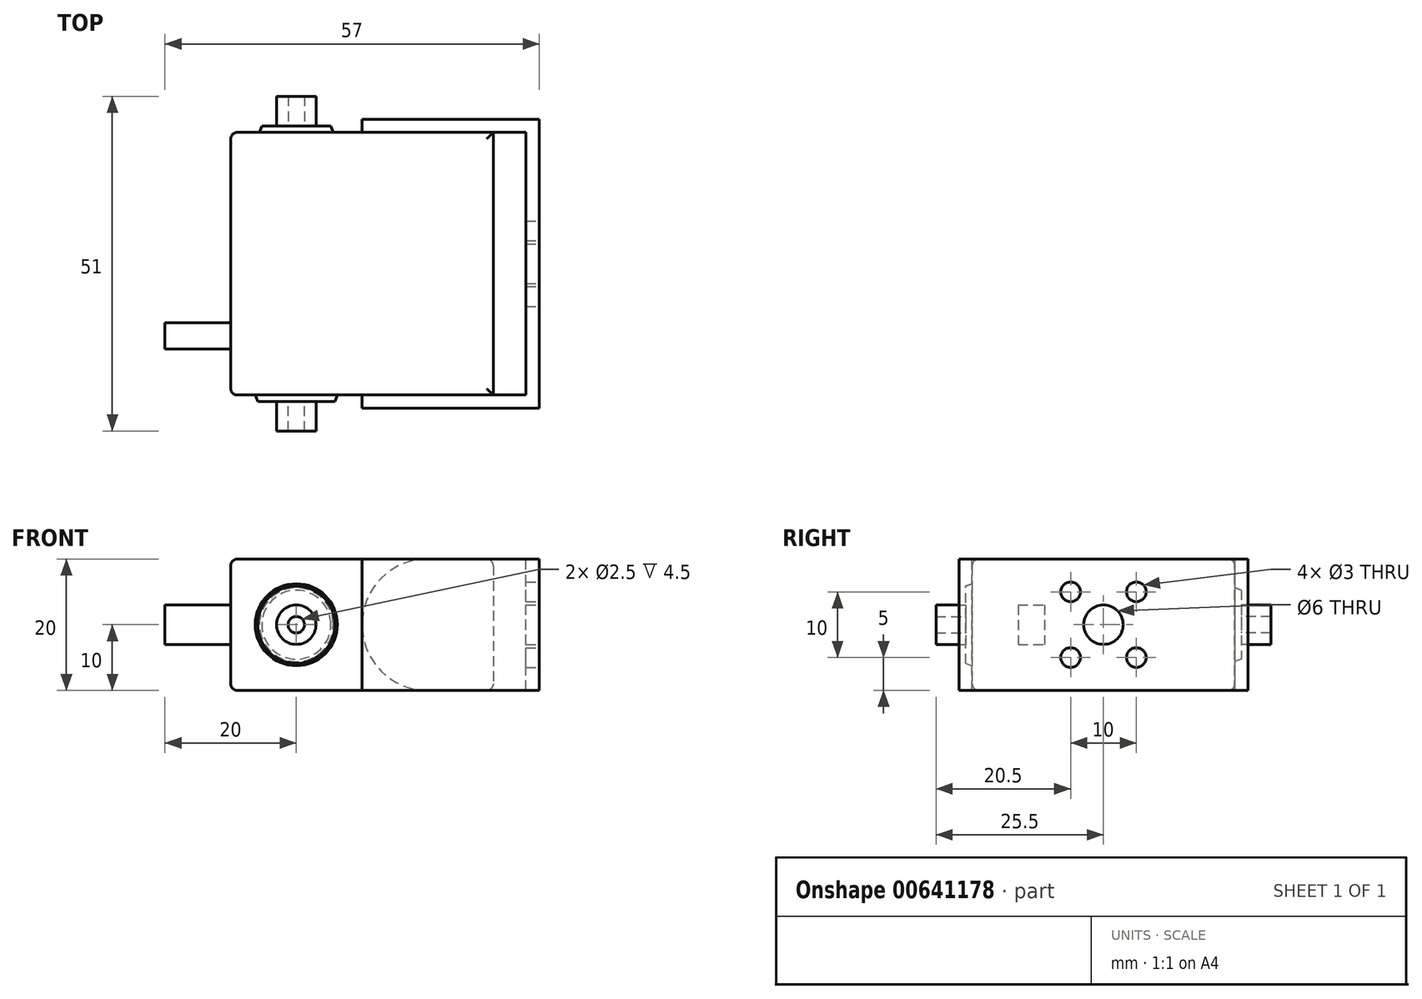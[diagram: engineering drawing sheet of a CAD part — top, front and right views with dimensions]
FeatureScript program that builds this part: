
annotation { "Feature Type Name" : "Feature", "Feature Type Description" : "" }
export const myFeature = defineFeature(function(context is Context, id is Id, definition is map)
    precondition{}
    {
        {
            var Q0;
            Q0=qCreatedBy(makeId("Top.planeOp"),FACE);
            var sketch = newSketch(context, id + "F0", { "sketchPlane" : qUnion([Q0])});
            skLineSegment(sketch, "E0.bottom", {"start": v(0, 0) * mm, "end": v(40, 0) * mm});
            skLineSegment(sketch, "E0.top", {"start": v(0, -40) * mm, "end": v(40, -40) * mm});
            skLineSegment(sketch, "E0.left", {"start": v(0, 0) * mm, "end": v(0, -40) * mm});
            skLineSegment(sketch, "E0.right", {"start": v(40, 0) * mm, "end": v(40, -40) * mm});
            skSolve(sketch);
        }
        {
            var Q0;
            Q0=makeQuery(id+"F0.imprint","IMPRINT",FACE,{"disambiguationData":[TD([[makeQuery(id+"F0.imprint","IMPRINT",EDGE,{"derivedFrom":sQuery(id+"F0.wireOp",EDGE,"E0.bottom")}),-1.0]])]});
            extrude(context, id + "F1", {"entities" : qUnion([Q0]), "depth" : 20 * mm, "offsetDistance" : 25 * mm});
        }
        {
            var Q0;
            Q0=makeQuery(id+"F1.opExtrude","CAP_FACE",FACE,{"disambiguationData":[OSD([sQuery(id+"F0.wireOp",EDGE,"E0.bottom"),sQuery(id+"F0.wireOp",EDGE,"E0.top"),sQuery(id+"F0.wireOp",EDGE,"E0.left"),sQuery(id+"F0.wireOp",EDGE,"E0.right")])],"isStart":false});
            var sketch = newSketch(context, id + "F2", { "sketchPlane" : qUnion([Q0])});
            skLineSegment(sketch, "E1", {"start": v(20, 0) * mm, "end": v(20, 2) * mm});
            skLineSegment(sketch, "E2", {"start": v(20, 2) * mm, "end": v(47, 2) * mm});
            skLineSegment(sketch, "E3", {"start": v(47, 2) * mm, "end": v(47, -42) * mm});
            skLineSegment(sketch, "E4", {"start": v(47, -42) * mm, "end": v(20, -42) * mm});
            skLineSegment(sketch, "E5", {"start": v(20, -42) * mm, "end": v(20, -40) * mm});
            skLineSegment(sketch, "E6", {"start": v(20, -40) * mm, "end": v(45, -40) * mm});
            skLineSegment(sketch, "E7", {"start": v(45, -40) * mm, "end": v(45, 0) * mm});
            skLineSegment(sketch, "E8", {"start": v(45, 0) * mm, "end": v(20, 0) * mm});
            skSolve(sketch);
        }
        {
            var Q0;
            {var subQ0=sQuery(id+"F2.wireOp",EDGE,"E1");Q0=makeQuery(id+"F2.imprint","IMPRINT",FACE,{"disambiguationData":[TD([[makeQuery(id+"F2.imprint","IMPRINT",EDGE,{"derivedFrom":subQ0}),-1.0]])]});}
            extrude(context, id + "F3", {"entities" : qUnion([Q0]), "oppositeDirection" : true, "depth" : 20 * mm, "offsetDistance" : 25 * mm});
        }
        {
            var Q0;
            Q0=makeQuery(id+"F3.opExtrude","SWEPT_FACE",FACE,{"disambiguationData":[OSD([sQuery(id+"F2.wireOp",EDGE,"E3")])]});
            var sketch = newSketch(context, id + "F4", { "sketchPlane" : qUnion([Q0])});
            skLineSegment(sketch, "E9", {"start": v(-20, 23.65) * mm, "end": v(-20, -9.22) * mm, "construction": true});
            skLineSegment(sketch, "E10", {"start": v(-39.5, 10) * mm, "end": v(6.88, 10) * mm, "construction": true});
            skCircle(sketch, "E11", {"center": v(-20, 10) * mm, "radius": 3 * mm});
            skCircle(sketch, "E12", {"center": v(-25, 15) * mm, "radius": 1.5 * mm});
            skCircle(sketch, "E13.MirrorC", {"center": v(-15, 15) * mm, "radius": 1.5 * mm});
            skCircle(sketch, "E14.MirrorC", {"center": v(-25, 5) * mm, "radius": 1.5 * mm});
            skCircle(sketch, "E15.MirrorC", {"center": v(-15, 5) * mm, "radius": 1.5 * mm});
            skSolve(sketch);
        }
        {
            var Q0;
            Q0 = qSketchRegion(id + "F4", true);
            extrude(context, id + "F5", {"entities" : qUnion([Q0]), "operationType" : NewBodyOperationType.REMOVE, "endBound" : BoundingType.UP_TO_NEXT, "oppositeDirection" : true, "depth" : 25 * mm, "offsetDistance" : 25 * mm});
        }
        {
            var Q0;
            Q0=makeQuery(id+"F1.opExtrude","SWEPT_FACE",FACE,{"disambiguationData":[OSD([sQuery(id+"F0.wireOp",EDGE,"E0.left")])]});
            var sketch = newSketch(context, id + "F6", { "sketchPlane" : qUnion([Q0])});
            skLineSegment(sketch, "E16.bottom", {"start": v(33, 13) * mm, "end": v(29, 13) * mm});
            skLineSegment(sketch, "E16.top", {"start": v(33, 7) * mm, "end": v(29, 7) * mm});
            skLineSegment(sketch, "E16.left", {"start": v(33, 13) * mm, "end": v(33, 7) * mm});
            skLineSegment(sketch, "E16.right", {"start": v(29, 13) * mm, "end": v(29, 7) * mm});
            skLineSegment(sketch, "E17", {"start": v(1.3, 10) * mm, "end": v(38.65, 10) * mm, "construction": true});
            skSolve(sketch);
        }
        {
            var Q0;
            Q0 = qSketchRegion(id + "F6", true);
            extrude(context, id + "F7", {"entities" : qUnion([Q0]), "depth" : 10 * mm, "offsetDistance" : 25 * mm});
        }
        {
            var Q0;
            Q0=makeQuery(id+"F1.opExtrude","SWEPT_FACE",FACE,{"disambiguationData":[OSD([sQuery(id+"F0.wireOp",EDGE,"E0.bottom")])]});
            var sketch = newSketch(context, id + "F8", { "sketchPlane" : qUnion([Q0])});
            skLineSegment(sketch, "E18", {"start": v(4.46, 10) * mm, "end": v(-49.62, 10) * mm, "construction": true});
            skCircle(sketch, "E19", {"center": v(-10, 10) * mm, "radius": 6.25 * mm});
            skSolve(sketch);
        }
        {
            var Q0;
            Q0=makeQuery(id+"F8.imprint","IMPRINT",FACE,{"disambiguationData":[TD([[makeQuery(id+"F8.imprint","IMPRINT",EDGE,{"derivedFrom":sQuery(id+"F8.wireOp",EDGE,"E19")}),1.0]])]});
            extrude(context, id + "F9", {"entities" : qUnion([Q0]), "depth" : 1 * mm, "offsetDistance" : 25 * mm});
        }
        {
            var Q0;
            Q0=makeQuery(id+"F9.opExtrude","CAP_FACE",FACE,{"disambiguationData":[OSD([sQuery(id+"F8.wireOp",EDGE,"E19")])],"isStart":false});
            var sketch = newSketch(context, id + "F10", { "sketchPlane" : qUnion([Q0])});
            skCircle(sketch, "E20", {"center": v(-10, 10) * mm, "radius": 3 * mm});
            skCircle(sketch, "E21", {"center": v(-10, 10) * mm, "radius": 1.25 * mm});
            skSolve(sketch);
        }
        {
            var Q0;
            Q0=makeQuery(id+"F10.imprint","IMPRINT",FACE,{"disambiguationData":[TD([[makeQuery(id+"F10.imprint","IMPRINT",EDGE,{"derivedFrom":sQuery(id+"F10.wireOp",EDGE,"E20")}),1.0]])]});
            extrude(context, id + "F11", {"entities" : qUnion([Q0]), "operationType" : NewBodyOperationType.ADD, "depth" : 4.5 * mm, "offsetDistance" : 25 * mm});
        }
        {
            var Q0;
            Q0=makeQuery(id+"F1.opExtrude","SWEPT_FACE",FACE,{"disambiguationData":[OSD([sQuery(id+"F0.wireOp",EDGE,"E0.bottom")])]});
            cPlane(context, id + "F12", {"entities" : qUnion([Q0]), "cplaneType" : CPlaneType.OFFSET, "offset" : 20 * mm, "oppositeDirection" : true, "width" : 150 * mm, "height" : 150 * mm});
        }
        {
            var Q0;
            Q0=makeQuery(id+"F9.opExtrude","SWEPT_BODY",BODY,{"disambiguationData":[OSD([sQuery(id+"F8.wireOp",EDGE,"E19")])]});
            var Q1;
            Q1=makeQuery(id+"F11.opExtrude","SWEPT_BODY",BODY,{"disambiguationData":[OSD([sQuery(id+"F10.wireOp",EDGE,"E20"),sQuery(id+"F10.wireOp",EDGE,"E21")])]});
            var Q2;
            Q2=qCreatedBy(id+"F12.planeOp",FACE);
            mirror(context, id + "F13", {"entities" : qUnion([Q0, Q1]), "mirrorPlane" : qUnion([Q2])});
        }
        {
            var Q0;
            Q0=makeQuery(id+"F1.opExtrude","CAP_EDGE",EDGE,{"disambiguationData":[OSD([sQuery(id+"F0.wireOp",EDGE,"E0.top")])],"isStart":false});
            var Q1;
            Q1=makeQuery(id+"F1.opExtrude","CAP_EDGE",EDGE,{"disambiguationData":[OSD([sQuery(id+"F0.wireOp",EDGE,"E0.top")])],"isStart":true});
            var Q2;
            Q2=makeQuery(id+"F1.opExtrude","CAP_EDGE",EDGE,{"disambiguationData":[OSD([sQuery(id+"F0.wireOp",EDGE,"E0.left")])],"isStart":false});
            var Q3;
            Q3=makeQuery(id+"F1.opExtrude","SWEPT_EDGE",EDGE,{"disambiguationData":[OSD([sQuery(id+"F0.wireOp",EDGE,"E0.top"),sQuery(id+"F0.wireOp",EDGE,"E0.left")])]});
            var Q4;
            Q4=makeQuery(id+"F1.opExtrude","CAP_EDGE",EDGE,{"disambiguationData":[OSD([sQuery(id+"F0.wireOp",EDGE,"E0.left")])],"isStart":true});
            var Q5;
            Q5=makeQuery(id+"F1.opExtrude","SWEPT_EDGE",EDGE,{"disambiguationData":[OSD([sQuery(id+"F0.wireOp",EDGE,"E0.bottom"),sQuery(id+"F0.wireOp",EDGE,"E0.left")])]});
            var Q6;
            Q6=makeQuery(id+"F1.opExtrude","CAP_EDGE",EDGE,{"disambiguationData":[OSD([sQuery(id+"F0.wireOp",EDGE,"E0.bottom")])],"isStart":false});
            var Q7;
            Q7=makeQuery(id+"F1.opExtrude","CAP_EDGE",EDGE,{"disambiguationData":[OSD([sQuery(id+"F0.wireOp",EDGE,"E0.bottom")])],"isStart":true});
            var Q8;
            Q8=makeQuery(id+"F1.opExtrude","CAP_EDGE",EDGE,{"disambiguationData":[OSD([sQuery(id+"F0.wireOp",EDGE,"E0.right")])],"isStart":false});
            var Q9;
            Q9=makeQuery(id+"F1.opExtrude","CAP_EDGE",EDGE,{"disambiguationData":[OSD([sQuery(id+"F0.wireOp",EDGE,"E0.right")])],"isStart":true});
            fillet(context, id + "F14", {"entities" : qUnion([Q0, Q1, Q2, Q3, Q4, Q5, Q6, Q7, Q8, Q9]), "radius" : 1 * mm, "tangentPropagation" : true, "allowEdgeOverflow" : false});
        }
        {
            var Q0;
            Q0=makeQuery(id+"F3.opExtrude","CAP_EDGE",EDGE,{"disambiguationData":[OSD([sQuery(id+"F2.wireOp",EDGE,"E1")])],"isStart":true});
            var Q1;
            Q1=makeQuery(id+"F3.opExtrude","CAP_EDGE",EDGE,{"disambiguationData":[OSD([sQuery(id+"F2.wireOp",EDGE,"E1")])],"isStart":false});
            fillet(context, id + "F15", {"entities" : qUnion([Q0, Q1]), "radius" : 10 * mm, "tangentPropagation" : true, "allowEdgeOverflow" : false});
        }
        {
            var Q0;
            Q0=makeQuery(id+"F13.opPattern","COPY",EDGE,{"derivedFrom":makeQuery(id+"F9.opExtrude","CAP_EDGE",EDGE,{"disambiguationData":[OSD([sQuery(id+"F8.wireOp",EDGE,"E19")])],"isStart":false}),"instanceName":"1"});
            chamfer(context, id + "F16", {"entities" : qUnion([Q0]), "chamferType" : ChamferType.OFFSET_ANGLE, "width" : 1 * mm, "oppositeDirection" : false, "angle" : 20 * degree, "tangentPropagation" : true});
        }
        {
            var Q0;
            Q0=makeQuery(id+"F9.opExtrude","CAP_EDGE",EDGE,{"disambiguationData":[OSD([sQuery(id+"F8.wireOp",EDGE,"E19")])],"isStart":false});
            chamfer(context, id + "F17", {"entities" : qUnion([Q0]), "chamferType" : ChamferType.OFFSET_ANGLE, "width" : 1 * mm, "oppositeDirection" : false, "angle" : 70 * degree});
        }
    });
